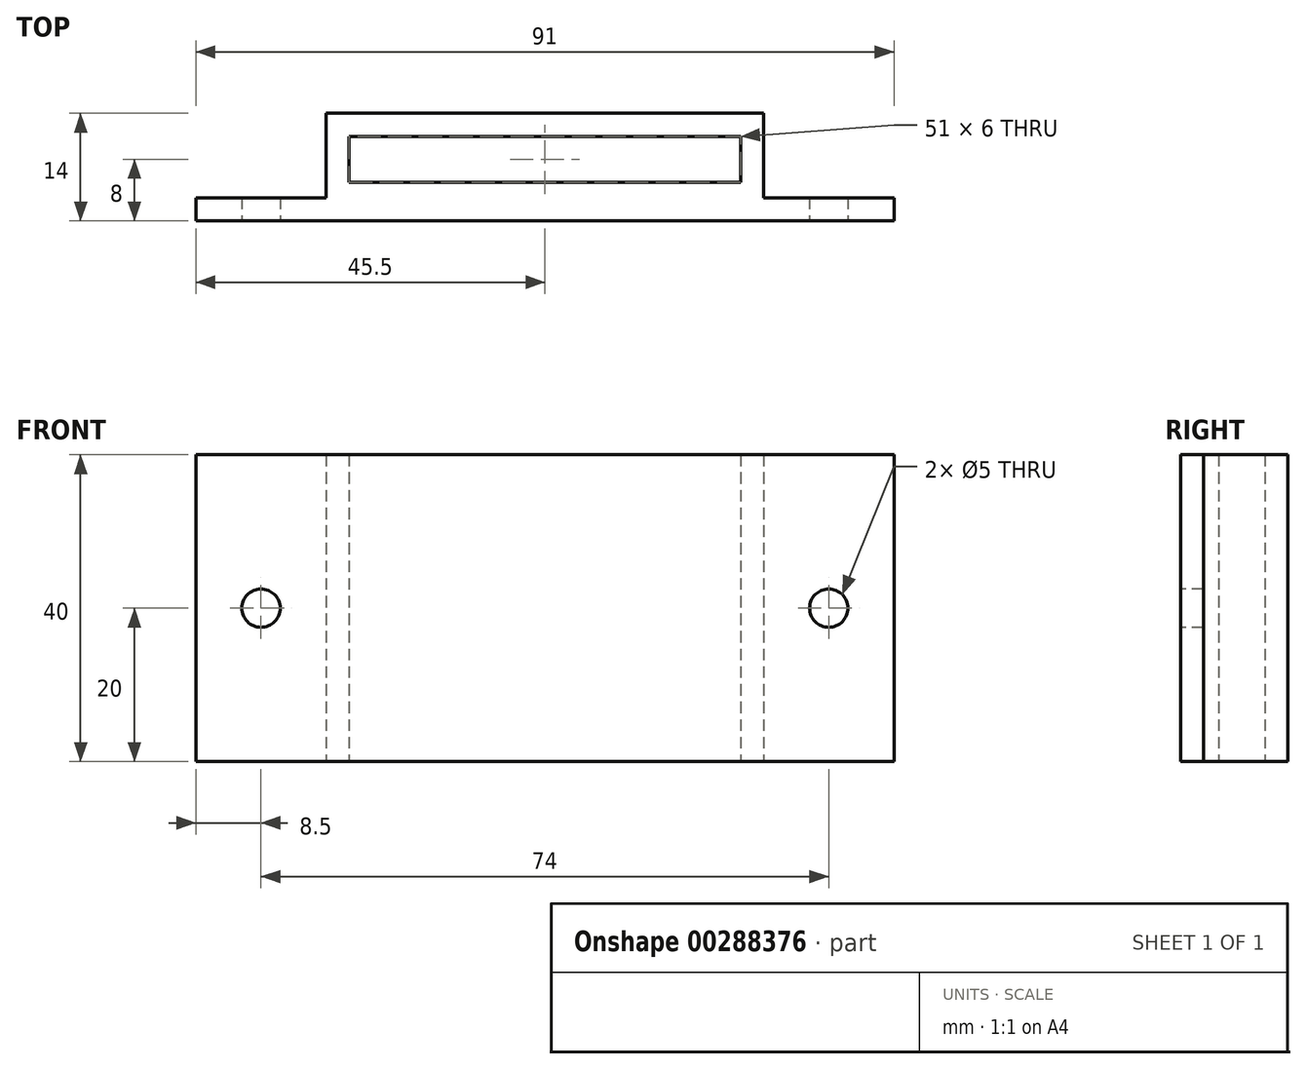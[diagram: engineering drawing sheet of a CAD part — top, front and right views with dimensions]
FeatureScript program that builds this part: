
annotation { "Feature Type Name" : "Feature", "Feature Type Description" : "" }
export const myFeature = defineFeature(function(context is Context, id is Id, definition is map)
    precondition{}
    {
        {
            var Q0;
            Q0=qCreatedBy(makeId("Top.planeOp"),FACE);
            var sketch = newSketch(context, id + "F0", { "sketchPlane" : qUnion([Q0])});
            skLineSegment(sketch, "E0", {"start": v(0, 0) * mm, "end": v(91, 0) * mm});
            skLineSegment(sketch, "E1", {"start": v(91, 0) * mm, "end": v(91, 3) * mm});
            skLineSegment(sketch, "E2", {"start": v(91, 3) * mm, "end": v(74, 3) * mm});
            skLineSegment(sketch, "E3", {"start": v(74, 3) * mm, "end": v(74, 14) * mm});
            skLineSegment(sketch, "E4", {"start": v(74, 14) * mm, "end": v(17, 14) * mm});
            skLineSegment(sketch, "E5", {"start": v(17, 14) * mm, "end": v(17, 3) * mm});
            skLineSegment(sketch, "E6", {"start": v(17, 3) * mm, "end": v(0, 3) * mm});
            skLineSegment(sketch, "E7", {"start": v(0, 3) * mm, "end": v(0, 0) * mm});
            skLineSegment(sketch, "E8.bottom", {"start": v(20, 5) * mm, "end": v(71, 5) * mm});
            skLineSegment(sketch, "E8.top", {"start": v(20, 11) * mm, "end": v(71, 11) * mm});
            skLineSegment(sketch, "E8.left", {"start": v(20, 5) * mm, "end": v(20, 11) * mm});
            skLineSegment(sketch, "E8.right", {"start": v(71, 5) * mm, "end": v(71, 11) * mm});
            skSolve(sketch);
        }
        {
            var Q0;
            Q0 = qSketchRegion(id + "F0", true);
            extrude(context, id + "F1", {"entities" : qUnion([Q0]), "depth" : 40 * mm, "offsetDistance" : 25 * mm});
        }
        {
            var Q0;
            Q0=makeQuery(id+"F1.opExtrude","SWEPT_FACE",FACE,{"disambiguationData":[OSD([sQuery(id+"F0.wireOp",EDGE,"E0")])]});
            var sketch = newSketch(context, id + "F2", { "sketchPlane" : qUnion([Q0])});
            skLineSegment(sketch, "E9", {"start": v(0, 20) * mm, "end": v(91, 20) * mm, "construction": true});
            skLineSegment(sketch, "E10", {"start": v(8.5, 40) * mm, "end": v(8.5, 0) * mm, "construction": true});
            skLineSegment(sketch, "E11", {"start": v(82.5, 40) * mm, "end": v(82.5, 0) * mm, "construction": true});
            skCircle(sketch, "E12", {"center": v(8.5, 20) * mm, "radius": 2.5 * mm});
            skCircle(sketch, "E13", {"center": v(82.5, 20) * mm, "radius": 2.5 * mm});
            skSolve(sketch);
        }
        {
            var Q0;
            Q0 = qSketchRegion(id + "F2", true);
            extrude(context, id + "F3", {"entities" : qUnion([Q0]), "operationType" : NewBodyOperationType.REMOVE, "oppositeDirection" : true, "depth" : 3 * mm, "offsetDistance" : 25 * mm});
        }
    });
